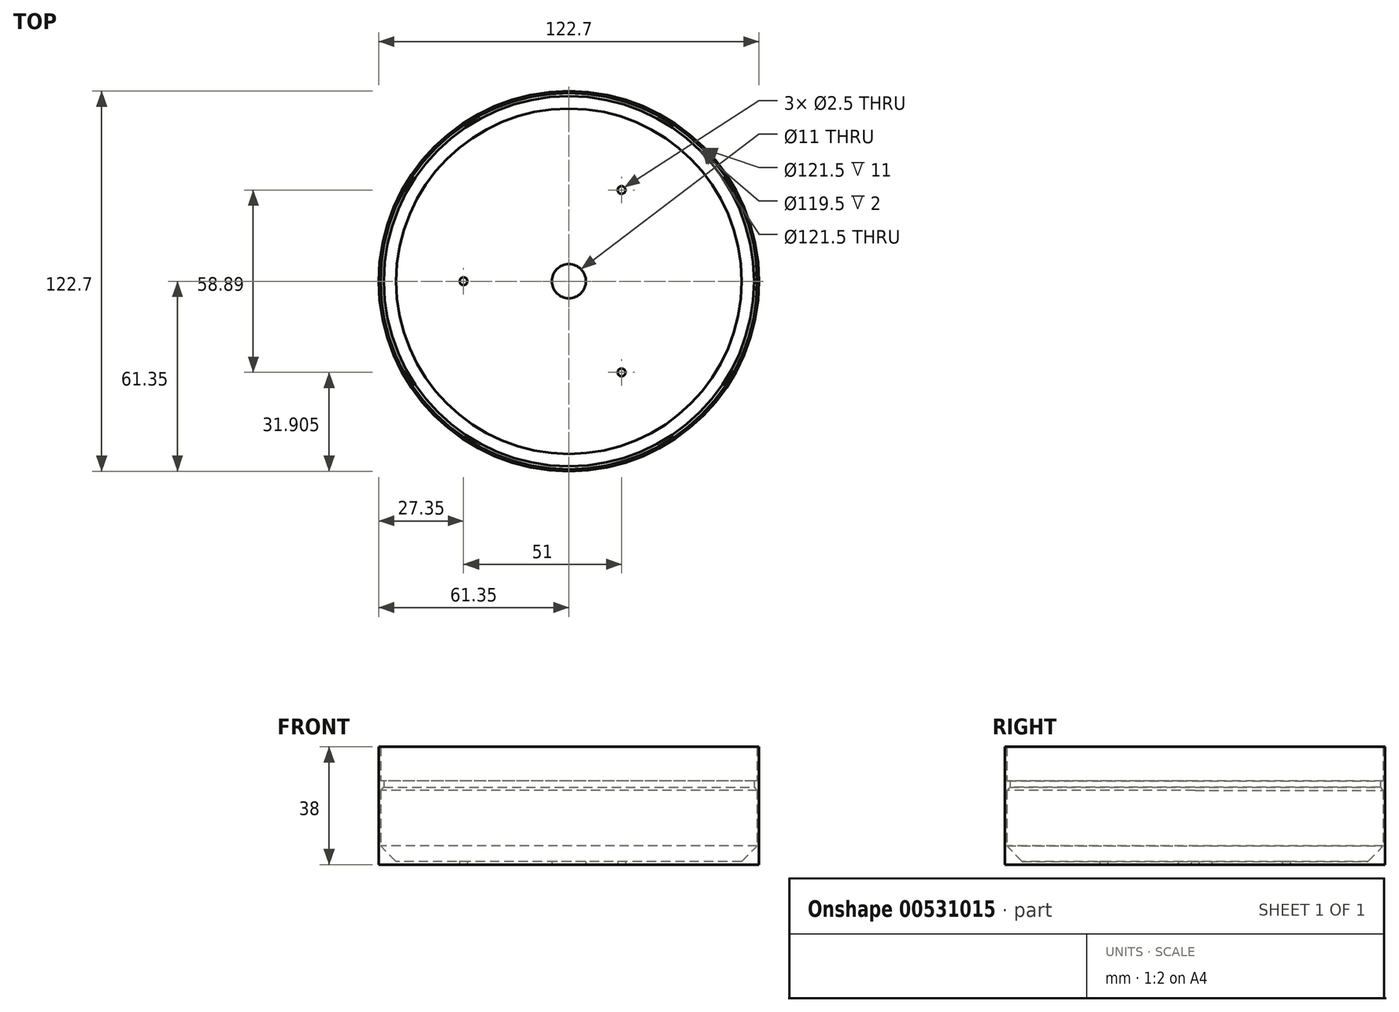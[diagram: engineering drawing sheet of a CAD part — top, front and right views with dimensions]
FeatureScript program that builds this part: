
annotation { "Feature Type Name" : "Feature", "Feature Type Description" : "" }
export const myFeature = defineFeature(function(context is Context, id is Id, definition is map)
    precondition{}
    {
        {
            var Q0;
            Q0=qCreatedBy(makeId("Top.planeOp"),FACE);
            var sketch = newSketch(context, id + "F0", { "sketchPlane" : qUnion([Q0])});
            skCircle(sketch, "E0", {"center": v(0, 0) * mm, "radius": 61.35 * mm});
            skLineSegment(sketch, "E1", {"start": v(0, 0) * mm, "end": v(-34, 0) * mm, "construction": true});
            skCircle(sketch, "E2", {"center": v(-34, 0) * mm, "radius": 1.25 * mm});
            skCircle(sketch, "E3.1.3", {"center": v(17, -29.44) * mm, "radius": 1.25 * mm});
            skCircle(sketch, "E3.2.3", {"center": v(17, 29.44) * mm, "radius": 1.25 * mm});
            skCircle(sketch, "E4", {"center": v(0, 0) * mm, "radius": 5.5 * mm});
            skSolve(sketch);
        }
        {
            var Q0;
            Q0=makeQuery(id+"F0.imprint","IMPRINT",FACE,{"disambiguationData":[TD([[makeQuery(id+"F0.imprint","IMPRINT",EDGE,{"derivedFrom":sQuery(id+"F0.wireOp",EDGE,"E0")}),1.0]])]});
            extrude(context, id + "F1", {"entities" : qUnion([Q0]), "depth" : 2 * mm, "offsetDistance" : 25 * mm});
        }
        {
            var Q0;
            Q0=makeQuery(id+"F1.opExtrude","CAP_FACE",FACE,{"disambiguationData":[OSD([sQuery(id+"F0.wireOp",EDGE,"E0"),sQuery(id+"F0.wireOp",EDGE,"E2"),sQuery(id+"F0.wireOp",EDGE,"E3.1.3"),sQuery(id+"F0.wireOp",EDGE,"E3.2.3"),sQuery(id+"F0.wireOp",EDGE,"E4")])],"isStart":false});
            var sketch = newSketch(context, id + "F2", { "sketchPlane" : qUnion([Q0])});
            skCircle(sketch, "E5", {"center": v(0, 0) * mm, "radius": 60.75 * mm});
            skCircle(sketch, "E6", {"center": v(0, 0) * mm, "radius": 61.35 * mm});
            skCircle(sketch, "E7", {"center": v(0, 0) * mm, "radius": 59.75 * mm});
            skSolve(sketch);
        }
        {
            var Q0;
            Q0 = qSketchRegion(id + "F2", true);
            extrude(context, id + "F3", {"entities" : qUnion([Q0]), "operationType" : NewBodyOperationType.ADD, "depth" : 37 * mm, "offsetDistance" : 25 * mm});
        }
        {
            var Q0;
            Q0=makeQuery(id+"F2.imprint","IMPRINT",FACE,{"disambiguationData":[TD([[makeQuery(id+"F2.imprint","IMPRINT",EDGE,{"derivedFrom":sQuery(id+"F2.wireOp",EDGE,"E5")}),1.0]])]});
            extrude(context, id + "F4", {"entities" : qUnion([Q0]), "operationType" : NewBodyOperationType.ADD, "depth" : 26 * mm, "offsetDistance" : 25 * mm});
        }
        {
            var Q0;
            Q0=makeQuery(id+"F2.imprint","IMPRINT",FACE,{"disambiguationData":[TD([[makeQuery(id+"F2.imprint","IMPRINT",EDGE,{"derivedFrom":sQuery(id+"F2.wireOp",EDGE,"E5")}),1.0]])]});
            extrude(context, id + "F5", {"entities" : qUnion([Q0]), "operationType" : NewBodyOperationType.REMOVE, "depth" : 25 * mm, "offsetDistance" : 25 * mm});
        }
        {
            var Q0;
            Q0=makeQuery(id+"F5.boolean.opBoolean","COPY",EDGE,{"derivedFrom":makeQuery(id+"F5.opExtrude","CAP_EDGE",EDGE,{"disambiguationData":[OSD([sQuery(id+"F2.wireOp",EDGE,"E5")])],"isStart":false})});
            chamfer(context, id + "F6", {"entities" : qUnion([Q0]), "width" : 2 * mm, "tangentPropagation" : true});
        }
        {
            var Q0;
            Q0=makeQuery(id+"F5.boolean.opBoolean","COPY",EDGE,{"derivedFrom":makeQuery(id+"F5.opExtrude","CAP_EDGE",EDGE,{"disambiguationData":[OSD([sQuery(id+"F2.wireOp",EDGE,"E5")])],"isStart":true})});
            chamfer(context, id + "F7", {"entities" : qUnion([Q0]), "width" : 5 * mm, "tangentPropagation" : true});
        }
        {
            var Q0;
            Q0=makeQuery(id+"F1.opExtrude","CAP_FACE",FACE,{"disambiguationData":[OSD([sQuery(id+"F0.wireOp",EDGE,"E0"),sQuery(id+"F0.wireOp",EDGE,"E2"),sQuery(id+"F0.wireOp",EDGE,"E3.1.3"),sQuery(id+"F0.wireOp",EDGE,"E3.2.3"),sQuery(id+"F0.wireOp",EDGE,"E4")])],"isStart":true});
            extrude(context, id + "F8", {"entities" : qUnion([Q0]), "operationType" : NewBodyOperationType.REMOVE, "oppositeDirection" : true, "depth" : 1 * mm, "offsetDistance" : 25 * mm});
        }
    });
